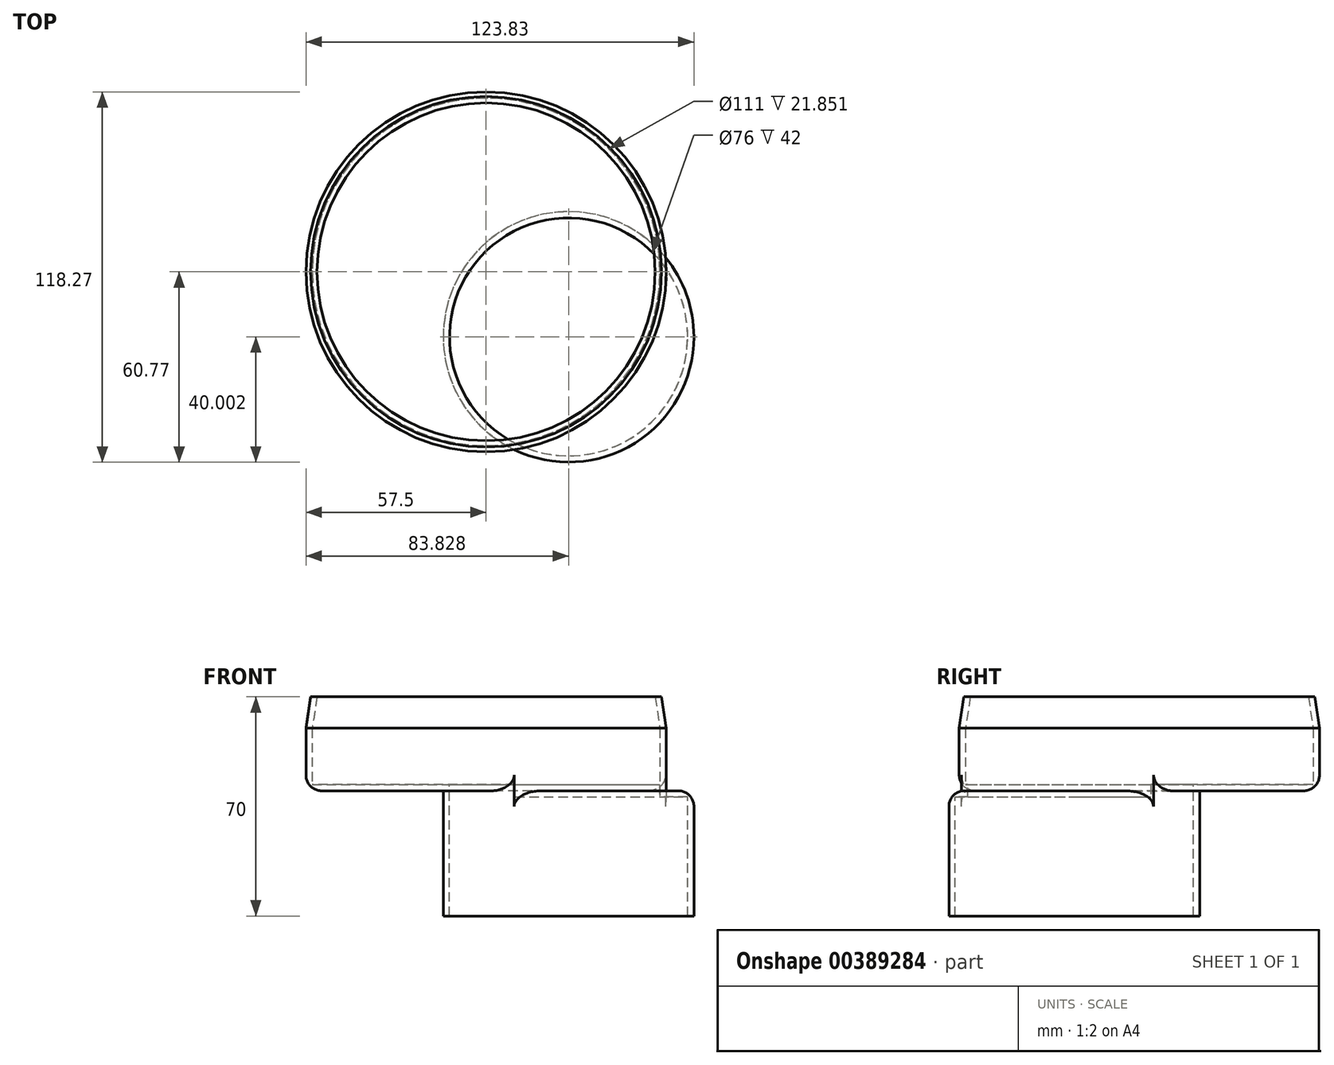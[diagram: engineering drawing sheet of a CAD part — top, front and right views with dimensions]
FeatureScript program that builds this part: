
annotation { "Feature Type Name" : "Feature", "Feature Type Description" : "" }
export const myFeature = defineFeature(function(context is Context, id is Id, definition is map)
    precondition{}
    {
        {
            var Q0;
            Q0=qCreatedBy(makeId("Front.planeOp"),FACE);
            var sketch = newSketch(context, id + "F0", { "sketchPlane" : qUnion([Q0])});
            skLineSegment(sketch, "E0.bottom", {"start": v(0, 0) * mm, "end": v(-57.5, 0) * mm});
            skLineSegment(sketch, "E0.top", {"start": v(0, 30) * mm, "end": v(-56, 30) * mm});
            skLineSegment(sketch, "E0.left", {"start": v(0, 0) * mm, "end": v(0, 30) * mm});
            skLineSegment(sketch, "E0.right", {"start": v(-57.5, 0) * mm, "end": v(-57.5, 20) * mm});
            skLineSegment(sketch, "E1", {"start": v(-56, 30) * mm, "end": v(-57.5, 20) * mm});
            skLineSegment(sketch, "E2", {"start": v(-56, 30) * mm, "end": v(-57.5, 30) * mm, "construction": true});
            skLineSegment(sketch, "E3", {"start": v(-57.5, 20) * mm, "end": v(-57.5, 30) * mm, "construction": true});
            skSolve(sketch);
        }
        {
            var Q0;
            Q0=makeQuery(id+"F0.imprint","IMPRINT",FACE,{"disambiguationData":[TD([[makeQuery(id+"F0.imprint","IMPRINT",EDGE,{"derivedFrom":sQuery(id+"F0.wireOp",EDGE,"E0.bottom")}),-1.0]])]});
            var Q1;
            Q1=sQuery(id+"F0.wireOp",EDGE,"E0.left");
            revolve(context, id + "F1", {"surfaceOperationType" : NewSurfaceOperationType.NEW, "entities" : qUnion([Q0]), "axis" : qUnion([Q1]), "revolveType" : RevolveType.FULL});
        }
        {
            var Q0;
            Q0=qCreatedBy(makeId("Top.planeOp"),FACE);
            var sketch = newSketch(context, id + "F2", { "sketchPlane" : qUnion([Q0])});
            skLineSegment(sketch, "E4.bottom", {"start": v(0, 57.5) * mm, "end": v(-44.5, 57.5) * mm, "construction": true});
            skLineSegment(sketch, "E4.top", {"start": v(0, 17.5) * mm, "end": v(-44.5, 17.5) * mm, "construction": true});
            skLineSegment(sketch, "E4.left", {"start": v(0, 57.5) * mm, "end": v(0, 17.5) * mm, "construction": true});
            skLineSegment(sketch, "E4.right", {"start": v(-44.5, 57.5) * mm, "end": v(-44.5, 17.5) * mm, "construction": true});
            skCircle(sketch, "E5", {"center": v(26.33, -20.77) * mm, "radius": 40 * mm});
            skSolve(sketch);
        }
        {
            var Q0;
            Q0 = qSketchRegion(id + "F2", true);
            extrude(context, id + "F3", {"entities" : qUnion([Q0]), "operationType" : NewBodyOperationType.ADD, "oppositeDirection" : true, "depth" : 40 * mm, "offsetDistance" : 25 * mm});
        }
        {
            var Q0;
            Q0=makeQuery(id+"F3.opExtrude","CAP_FACE",FACE,{"disambiguationData":[OSD([sQuery(id+"F2.wireOp",EDGE,"E5")])],"isStart":false});
            var Q1;
            Q1=makeQuery(id+"F1.opRevolve","SWEPT_FACE",FACE,{"disambiguationData":[OSD([sQuery(id+"F0.wireOp",EDGE,"E0.top")])]});
            shell(context, id + "F4", {"entities" : qUnion([Q0, Q1]), "thickness" : 2 * mm});
        }
        {
            var Q0;
            {var subQ0=sQuery(id+"F0.wireOp",EDGE,"E0.right");Q0=makeQuery(id+"F3.boolean.opBoolean","SPLIT",EDGE,{"disambiguationData":[topologyDisambiguationEdgeConnected([makeQuery(id+"F3.opExtrude","CAP_FACE",FACE,{"disambiguationData":[OSD([sQuery(id+"F2.wireOp",EDGE,"E5")])],"isStart":true})])],"derivedFrom":makeQuery(id+"F1.opRevolve","SWEPT_EDGE",EDGE,{"disambiguationData":[OSD([sQuery(id+"F0.wireOp",EDGE,"E0.bottom"),subQ0])]})});}
            fillet(context, id + "F5", {"entities" : qUnion([Q0]), "tangentPropagation" : true, "radius" : 5 * mm, "defaultsChanged" : false, "vertexSettings" : [], "allowEdgeOverflow" : false});
        }
        {
            var Q0;
            {var subQ0=sQuery(id+"F2.wireOp",EDGE,"E5");Q0=makeQuery(id+"F3.boolean.opBoolean","SPLIT",EDGE,{"disambiguationData":[topologyDisambiguationEdgeConnected([makeQuery(id+"F1.opRevolve","SWEPT_FACE",FACE,{"disambiguationData":[OSD([sQuery(id+"F0.wireOp",EDGE,"E0.bottom")])]})])],"derivedFrom":makeQuery(id+"F3.opExtrude","CAP_EDGE",EDGE,{"disambiguationData":[OSD([subQ0])],"isStart":true})});}
            fillet(context, id + "F6", {"entities" : qUnion([Q0]), "tangentPropagation" : true, "radius" : 5 * mm, "defaultsChanged" : false, "vertexSettings" : [], "allowEdgeOverflow" : false});
        }
    });
